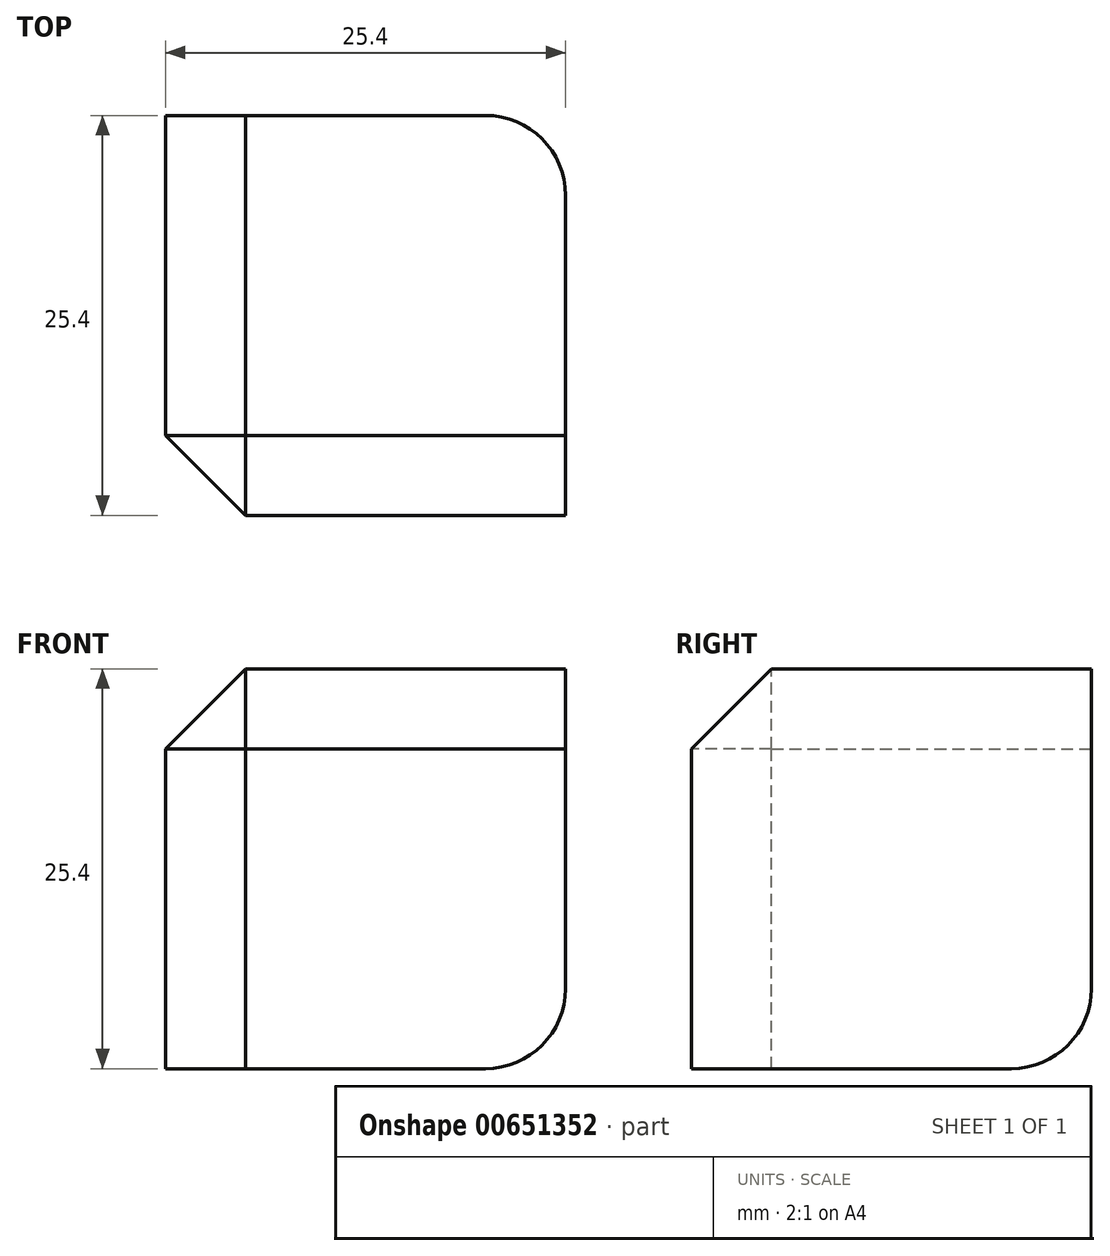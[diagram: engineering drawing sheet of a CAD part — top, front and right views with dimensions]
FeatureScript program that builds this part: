
annotation { "Feature Type Name" : "Feature", "Feature Type Description" : "" }
export const myFeature = defineFeature(function(context is Context, id is Id, definition is map)
    precondition{}
    {
        {
            var Q0;
            Q0=qCreatedBy(makeId("Front.planeOp"),FACE);
            var sketch = newSketch(context, id + "F0", { "sketchPlane" : qUnion([Q0])});
            skLineSegment(sketch, "E0.bottom", {"start": v(12.7, 12.7) * mm, "end": v(-12.7, 12.7) * mm});
            skLineSegment(sketch, "E0.top", {"start": v(12.7, -12.7) * mm, "end": v(-12.7, -12.7) * mm});
            skLineSegment(sketch, "E0.left", {"start": v(12.7, 12.7) * mm, "end": v(12.7, -12.7) * mm});
            skLineSegment(sketch, "E0.right", {"start": v(-12.7, 12.7) * mm, "end": v(-12.7, -12.7) * mm});
            skPoint(sketch, "E0.middle", {"position": v(0, 0) * mm});
            skSolve(sketch);
        }
        {
            var Q0;
            Q0 = qSketchRegion(id + "F0", true);
            extrude(context, id + "F1", {"entities" : qUnion([Q0]), "endBound" : BoundingType.SYMMETRIC, "depth" : 25.4 * mm, "offsetDistance" : 25.4 * mm});
        }
        {
            var Q0;
            Q0=makeQuery(id+"F1.opExtrude","CAP_EDGE",EDGE,{"disambiguationData":[OSD([sQuery(id+"F0.wireOp",EDGE,"E0.bottom")])],"isStart":false});
            var Q1;
            Q1=makeQuery(id+"F1.opExtrude","SWEPT_EDGE",EDGE,{"disambiguationData":[OSD([sQuery(id+"F0.wireOp",EDGE,"E0.bottom"),sQuery(id+"F0.wireOp",EDGE,"E0.right")])]});
            var Q2;
            Q2=makeQuery(id+"F1.opExtrude","CAP_EDGE",EDGE,{"disambiguationData":[OSD([sQuery(id+"F0.wireOp",EDGE,"E0.right")])],"isStart":false});
            chamfer(context, id + "F2", {"entities" : qUnion([Q0, Q1, Q2]), "width" : 5.08 * mm, "tangentPropagation" : true});
        }
        {
            var Q0;
            Q0=makeQuery(id+"F1.opExtrude","CAP_EDGE",EDGE,{"disambiguationData":[OSD([sQuery(id+"F0.wireOp",EDGE,"E0.left")])],"isStart":true});
            var Q1;
            Q1=makeQuery(id+"F1.opExtrude","SWEPT_EDGE",EDGE,{"disambiguationData":[OSD([sQuery(id+"F0.wireOp",EDGE,"E0.top"),sQuery(id+"F0.wireOp",EDGE,"E0.left")])]});
            var Q2;
            Q2=makeQuery(id+"F1.opExtrude","CAP_EDGE",EDGE,{"disambiguationData":[OSD([sQuery(id+"F0.wireOp",EDGE,"E0.top")])],"isStart":true});
            fillet(context, id + "F3", {"entities" : qUnion([Q0, Q1, Q2]), "radius" : 5.08 * mm, "tangentPropagation" : true, "allowEdgeOverflow" : false});
        }
    });
